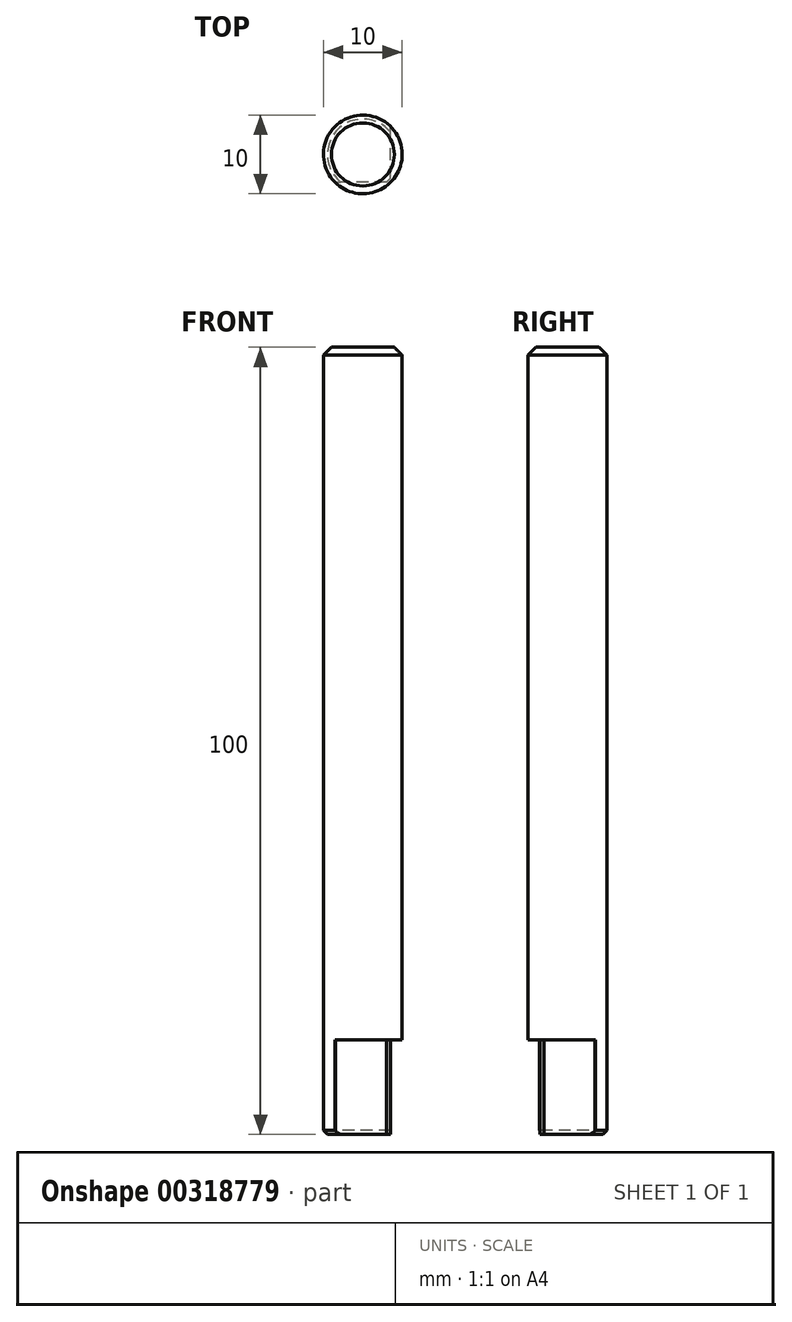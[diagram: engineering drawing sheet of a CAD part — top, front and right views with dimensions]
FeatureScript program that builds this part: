
annotation { "Feature Type Name" : "Feature", "Feature Type Description" : "" }
export const myFeature = defineFeature(function(context is Context, id is Id, definition is map)
    precondition{}
    {
        {
            var Q0;
            Q0=qCreatedBy(makeId("Top.planeOp"),FACE);
            var sketch = newSketch(context, id + "F0", { "sketchPlane" : qUnion([Q0])});
            skCircle(sketch, "E0", {"center": v(0, 0) * mm, "radius": 5 * mm});
            skSolve(sketch);
        }
        {
            var Q0;
            Q0 = qSketchRegion(id + "F0", true);
            extrude(context, id + "F1", {"entities" : qUnion([Q0]), "depth" : 100 * mm, "offsetDistance" : 25 * mm});
        }
        {
            var Q0;
            Q0=makeQuery(id+"F1.opExtrude","CAP_FACE",FACE,{"disambiguationData":[OSD([sQuery(id+"F0.wireOp",EDGE,"E0")])],"isStart":true});
            var sketch = newSketch(context, id + "F2", { "sketchPlane" : qUnion([Q0])});
            skLineSegment(sketch, "E1.bottom", {"start": v(3.5, 3.5) * mm, "end": v(-3.5, 3.5) * mm});
            skLineSegment(sketch, "E1.top", {"start": v(3.5, -3.5) * mm, "end": v(-3.5, -3.5) * mm});
            skLineSegment(sketch, "E1.left", {"start": v(3.5, 3.5) * mm, "end": v(3.5, -3.5) * mm});
            skLineSegment(sketch, "E1.right", {"start": v(-3.5, 3.5) * mm, "end": v(-3.5, -3.5) * mm});
            skPoint(sketch, "E1.middle", {"position": v(0, 0) * mm});
            skLineSegment(sketch, "E2", {"start": v(0, 3.5) * mm, "end": v(0, 5) * mm, "construction": true});
            skLineSegment(sketch, "E3", {"start": v(-3.5, 3.5) * mm, "end": v(-3.54, 3.53) * mm});
            skLineSegment(sketch, "E4", {"start": v(3.5, -3.5) * mm, "end": v(3.53, -3.54) * mm});
            skSolve(sketch);
        }
        {
            var Q0;
            Q0=makeQuery(id+"F2.imprint","IMPRINT",FACE,{"disambiguationData":[TD([[makeQuery(id+"F2.imprint","IMPRINT",EDGE,{"derivedFrom":sQuery(id+"F2.wireOp",EDGE,"E1.bottom")}),-1.0]])]});
            extrude(context, id + "F3", {"entities" : qUnion([Q0]), "operationType" : NewBodyOperationType.REMOVE, "oppositeDirection" : true, "depth" : 12 * mm, "offsetDistance" : 25 * mm});
        }
        {
            var Q0;
            Q0=makeQuery(id+"F1.opExtrude","CAP_FACE",FACE,{"disambiguationData":[OSD([sQuery(id+"F0.wireOp",EDGE,"E0")])],"isStart":false});
            chamfer(context, id + "F4", {"entities" : qUnion([Q0]), "width" : 1 * mm, "tangentPropagation" : true});
        }
        {
            var Q0;
            Q0=makeQuery(id+"F3.boolean.opBoolean","COPY",EDGE,{"derivedFrom":makeQuery(id+"F3.opExtrude","CAP_EDGE",EDGE,{"disambiguationData":[OSD([sQuery(id+"F2.wireOp",EDGE,"E1.bottom")])],"isStart":true})});
            var Q1;
            Q1=makeQuery(id+"F3.boolean.opBoolean","COPY",EDGE,{"derivedFrom":makeQuery(id+"F3.opExtrude","CAP_EDGE",EDGE,{"disambiguationData":[OSD([sQuery(id+"F2.wireOp",EDGE,"E1.left")])],"isStart":true})});
            var Q2;
            Q2=makeQuery(id+"F3.boolean.opBoolean","COPY",EDGE,{"derivedFrom":makeQuery(id+"F3.opExtrude","SWEPT_EDGE",EDGE,{"disambiguationData":[OSD([sQuery(id+"F2.wireOp",EDGE,"E1.bottom"),sQuery(id+"F2.wireOp",EDGE,"E1.left")])]})});
            chamfer(context, id + "F5", {"entities" : qUnion([Q0, Q1, Q2]), "width" : 0.5 * mm, "tangentPropagation" : true});
        }
        {
            var Q0;
            Q0=makeQuery(id+"F1.opExtrude","CAP_EDGE",EDGE,{"disambiguationData":[OSD([sQuery(id+"F0.wireOp",EDGE,"E0")])],"isStart":true});
            var Q1;
            Q1=makeQuery(id+"F3.boolean.opBoolean","COPY",EDGE,{"derivedFrom":makeQuery(id+"F3.opExtrude","CAP_EDGE",EDGE,{"disambiguationData":[OSD([sQuery(id+"F0.wireOp",EDGE,"E0")])],"isStart":false})});
            chamfer(context, id + "F6", {"entities" : qUnion([Q0, Q1]), "width" : 0.5 * mm, "tangentPropagation" : true});
        }
    });
